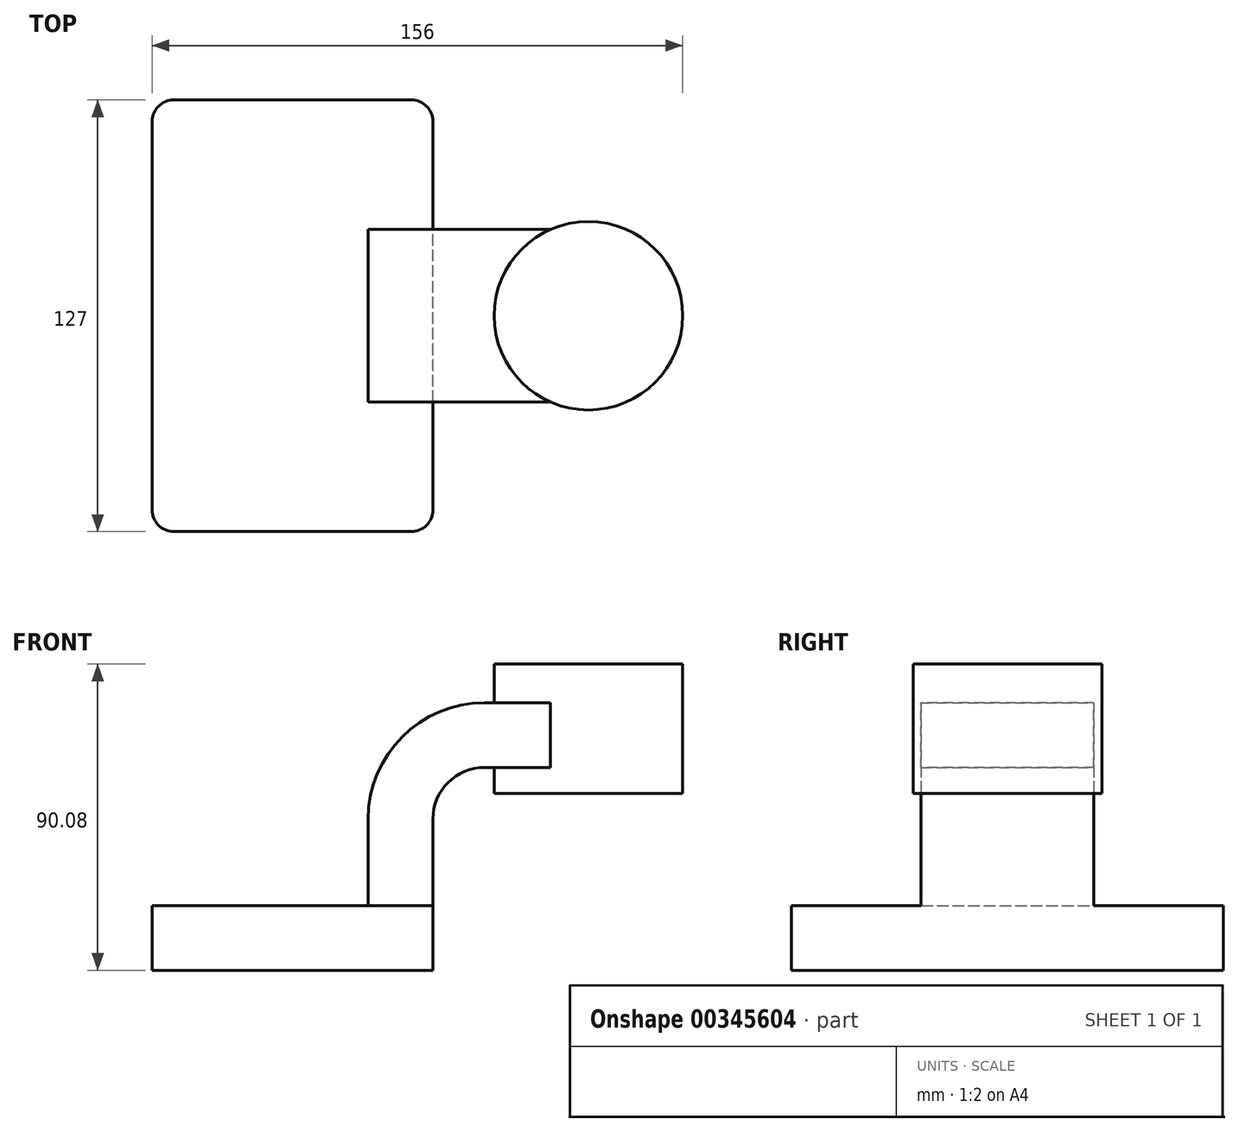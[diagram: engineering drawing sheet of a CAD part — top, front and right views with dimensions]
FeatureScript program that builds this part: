
annotation { "Feature Type Name" : "Feature", "Feature Type Description" : "" }
export const myFeature = defineFeature(function(context is Context, id is Id, definition is map)
    precondition{}
    {
        {
            var Q0;
            Q0=qCreatedBy(makeId("Front.planeOp"),FACE);
            var sketch = newSketch(context, id + "F0", { "sketchPlane" : qUnion([Q0])});
            skLineSegment(sketch, "E0.bottom", {"start": v(41.27, 9.53) * mm, "end": v(-41.28, 9.53) * mm});
            skLineSegment(sketch, "E0.top", {"start": v(41.28, -9.52) * mm, "end": v(-41.27, -9.52) * mm});
            skLineSegment(sketch, "E0.left", {"start": v(41.28, 9.53) * mm, "end": v(41.28, -9.52) * mm});
            skLineSegment(sketch, "E0.right", {"start": v(-41.28, 9.53) * mm, "end": v(-41.27, -9.52) * mm});
            skPoint(sketch, "E0.middle", {"position": v(0, 0) * mm});
            skLineSegment(sketch, "E1.bottom", {"start": v(76.63, 80.55) * mm, "end": v(114.73, 80.55) * mm});
            skLineSegment(sketch, "E1.top", {"start": v(76.63, 42.45) * mm, "end": v(114.73, 42.45) * mm});
            skLineSegment(sketch, "E1.left", {"start": v(76.63, 80.55) * mm, "end": v(76.63, 42.45) * mm});
            skLineSegment(sketch, "E1.right", {"start": v(114.73, 80.55) * mm, "end": v(114.73, 42.45) * mm});
            skPoint(sketch, "E1.middle", {"position": v(95.68, 61.5) * mm});
            skLineSegment(sketch, "E2", {"start": v(41.27, 9.53) * mm, "end": v(41.27, 34.93) * mm});
            skArc(sketch, "E3", {"start": v(41.27, 34.93) * mm, "mid": v(45.74, 45.7) * mm, "end": v(56.51, 50.17) * mm});
            skLineSegment(sketch, "E4", {"start": v(56.51, 50.17) * mm, "end": v(87, 50.17) * mm});
            skLineSegment(sketch, "E5.0", {"start": v(56.51, 69.22) * mm, "end": v(87, 69.22) * mm});
            skArc(sketch, "E5.1", {"start": v(22.22, 34.93) * mm, "mid": v(32.27, 59.17) * mm, "end": v(56.51, 69.22) * mm});
            skLineSegment(sketch, "E5.2", {"start": v(22.22, 9.53) * mm, "end": v(22.22, 34.93) * mm});
            skLineSegment(sketch, "E6", {"start": v(87, 80.55) * mm, "end": v(87, 42.45) * mm});
            skFitSpline(sketch, "E7", {"points": [v(-41.28, 9.52) * mm, v(56.51, 69.22) * mm], "startDerivative": vector(0.45, 116.05) * mm, "endDerivative": vector(126.41, -0.3) * mm});
            skSolve(sketch);
        }
        {
            var Q0;
            Q0=makeQuery(id+"F0.imprint","IMPRINT",FACE,{"disambiguationData":[TD([[makeQuery(id+"F0.imprint","IMPRINT",EDGE,{"derivedFrom":sQuery(id+"F0.wireOp",EDGE,"E0.top")}),-1.0]])]});
            extrude(context, id + "F1", {"entities" : qUnion([Q0]), "endBound" : BoundingType.SYMMETRIC, "depth" : 127 * mm});
        }
        {
            var Q0;
            {var subQ1=sQuery(id+"F0.wireOp",EDGE,"E2");Q0=makeQuery(id+"F0.imprint","IMPRINT",FACE,{"disambiguationData":[TD([[makeQuery(id+"F0.imprint","IMPRINT",EDGE,{"derivedFrom":subQ1}),1.0]])]});}
            extrude(context, id + "F2", {"entities" : qUnion([Q0]), "operationType" : NewBodyOperationType.ADD, "endBound" : BoundingType.SYMMETRIC, "depth" : 50.8 * mm});
        }
        {
            var Q0;
            Q0=makeQuery(id+"F0.imprint","IMPRINT",FACE,{"disambiguationData":[TD([[makeQuery(id+"F0.imprint","IMPRINT",EDGE,{"derivedFrom":sQuery(id+"F0.wireOp",EDGE,"E5.1")}),1.0]])]});
            extrude(context, id + "F3", {"entities" : qUnion([Q0]), "operationType" : NewBodyOperationType.ADD, "endBound" : BoundingType.SYMMETRIC, "depth" : 15.88 * mm});
        }
        {
            var Q0;
            {var subQ0=sQuery(id+"F0.wireOp",EDGE,"E1.right");Q0=makeQuery(id+"F0.imprint","IMPRINT",FACE,{"disambiguationData":[TD([[makeQuery(id+"F0.imprint","IMPRINT",EDGE,{"derivedFrom":subQ0}),-1.0]])]});}
            var Q1;
            Q1=sQuery(id+"F0.wireOp",EDGE,"E6");
            revolve(context, id + "F4", {"operationType" : NewBodyOperationType.ADD, "entities" : qUnion([Q0]), "axis" : qUnion([Q1]), "revolveType" : RevolveType.FULL});
        }
        {
            var Q0;
            Q0=makeQuery(id+"F1.opExtrude","CAP_EDGE",EDGE,{"disambiguationData":[OSD([sQuery(id+"F0.wireOp",EDGE,"E0.right")])],"isStart":true});
            var Q1;
            Q1=makeQuery(id+"F1.opExtrude","CAP_EDGE",EDGE,{"disambiguationData":[OSD([sQuery(id+"F0.wireOp",EDGE,"E0.right")])],"isStart":false});
            var Q2;
            Q2=makeQuery(id+"F1.opExtrude","CAP_EDGE",EDGE,{"disambiguationData":[OSD([sQuery(id+"F0.wireOp",EDGE,"E0.left")])],"isStart":true});
            var Q3;
            Q3=makeQuery(id+"F1.opExtrude","CAP_EDGE",EDGE,{"disambiguationData":[OSD([sQuery(id+"F0.wireOp",EDGE,"E0.left")])],"isStart":false});
            fillet(context, id + "F5", {"entities" : qUnion([Q0, Q1, Q2, Q3]), "radius" : 6.35 * mm, "tangentPropagation" : true, "allowEdgeOverflow" : false});
        }
    });
